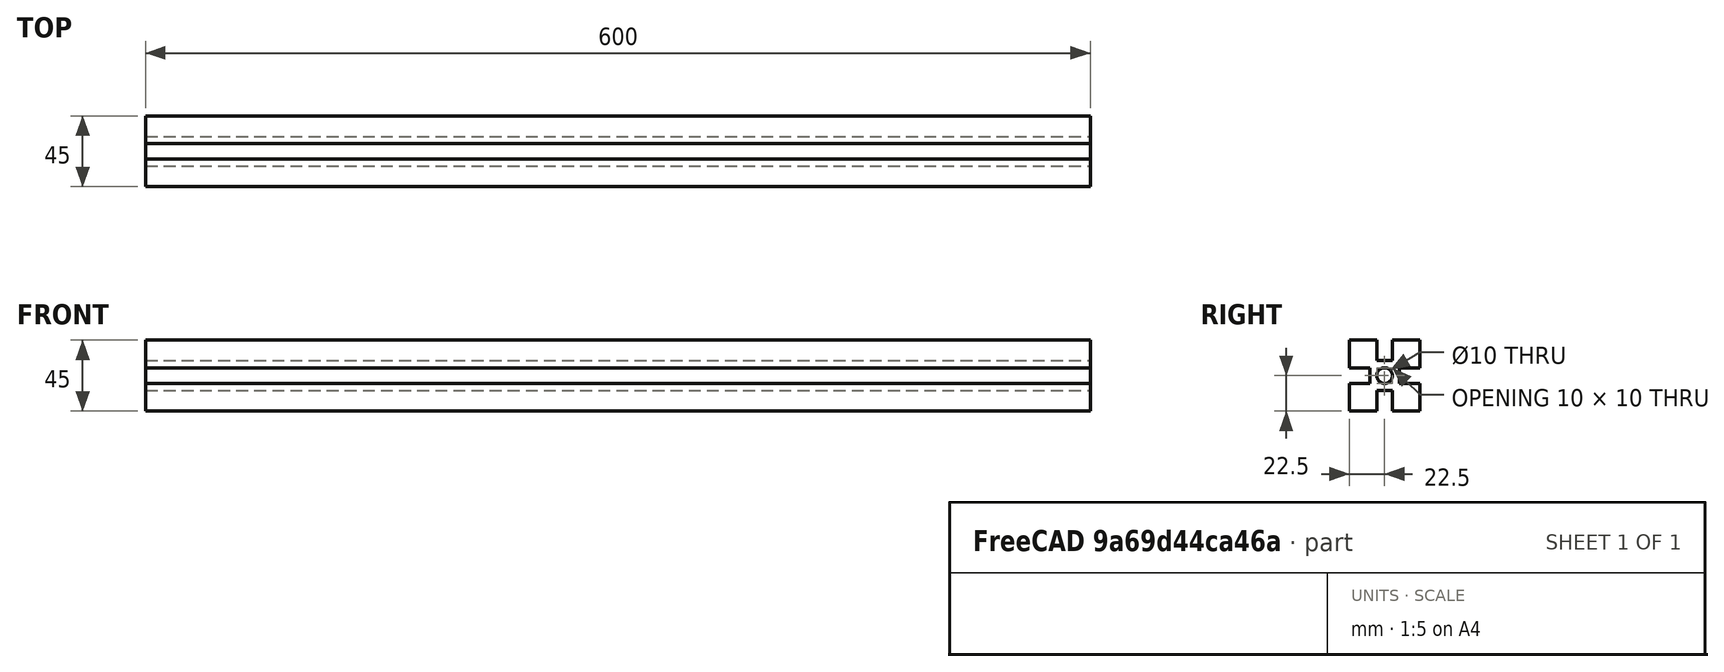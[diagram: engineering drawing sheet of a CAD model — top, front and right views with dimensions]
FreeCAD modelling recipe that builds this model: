
FCSTD DOCUMENT  (FreeCAD 1.0R39109 (Git))
Label: vslot 45x45x600
License: All rights reserved
LicenseURL: https://en.wikipedia.org/wiki/All_rights_reserved
objects: PartDesign::Pocket×2, Part::Feature×1, PartDesign::FeatureBase×1, PartDesign::Pad×1, PartDesign::Body×1
note: 13 computed .brp shape members not serialized (recipe doc carries the construction recipe); baked Part::Feature solids carry a one-line shape summary decoded from their .brp

FEATURE [Part::Feature] Part__Feature  label="1"
  shape: bbox 1000 x 45 x 45 mm, 24 faces (baked)
FEATURE [PartDesign::FeatureBase] BaseFeature
  BaseFeature = -> Part__Feature
  Suppressed = false
FEATURE [PartDesign::Pad] Pad
  BaseFeature = -> BaseFeature
  Direction = (1,0,0)
  Length = 220
  Length2 = 10
  Profile = -> BaseFeature [Face24]
  Refine = true
  Suppressed = false
  Type = 0
FEATURE [PartDesign::Pocket] Pocket
  BaseFeature = -> Pad
  Direction = (-1,0,0)
  Length = 140
  Length2 = 5
  Profile = -> Pad [Face3]
  Refine = true
  Suppressed = false
  Type = 0
FEATURE [PartDesign::Pocket] Pocket001
  BaseFeature = -> Pocket
  Direction = (-1,0,0)
  Length = 480
  Length2 = 5
  Profile = -> Pocket [Face23]
  Refine = true
  Suppressed = false
  Type = 0
FEATURE [PartDesign::Body] Body
  AllowCompound = false
  BaseFeature = -> Part__Feature
  Group = -> [BaseFeature,Pad,Pocket,Pocket001]
  Origin = -> Origin
  Tip = -> Pocket001
